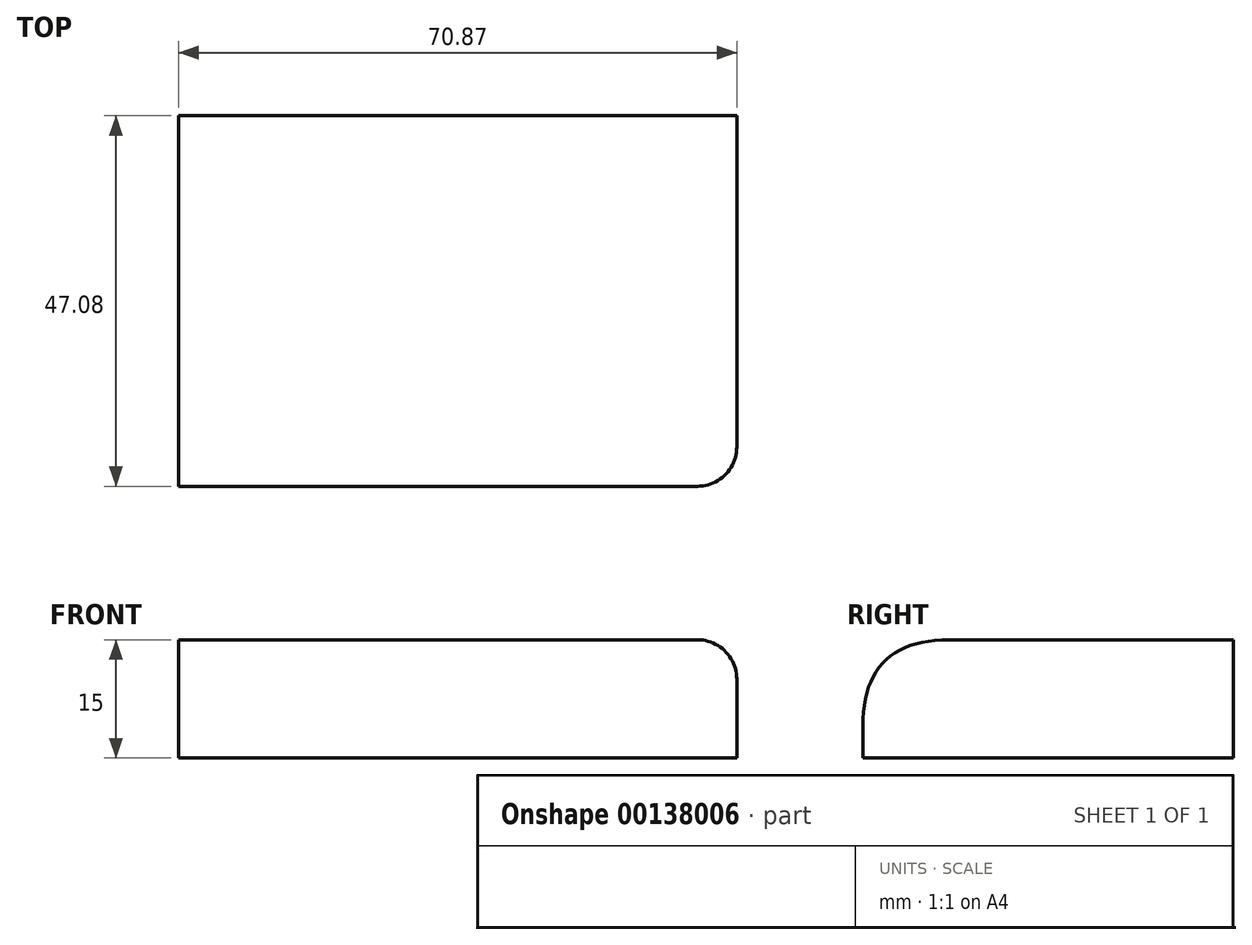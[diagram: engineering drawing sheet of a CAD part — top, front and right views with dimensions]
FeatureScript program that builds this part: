
annotation { "Feature Type Name" : "Feature", "Feature Type Description" : "" }
export const myFeature = defineFeature(function(context is Context, id is Id, definition is map)
    precondition{}
    {
        {
            var Q0;
            Q0=qCreatedBy(makeId("Top.planeOp"),FACE);
            var sketch = newSketch(context, id + "F0", { "sketchPlane" : qUnion([Q0])});
            skLineSegment(sketch, "E0.bottom", {"start": v(-36.05, -47.08) * mm, "end": v(34.82, -47.08) * mm});
            skLineSegment(sketch, "E0.top", {"start": v(-36.05, 0) * mm, "end": v(34.82, 0) * mm});
            skLineSegment(sketch, "E0.left", {"start": v(-36.05, -47.08) * mm, "end": v(-36.05, 0) * mm});
            skLineSegment(sketch, "E0.right", {"start": v(34.82, -47.08) * mm, "end": v(34.82, 0) * mm});
            skSolve(sketch);
        }
        {
            var Q0;
            Q0 = qSketchRegion(id + "F0", true);
            extrude(context, id + "F1", {"entities" : qUnion([Q0]), "depth" : 15 * mm});
        }
        {
            var Q0;
            Q0=makeQuery(id+"F1.opExtrude","CAP_EDGE",EDGE,{"disambiguationData":[OSD([sQuery(id+"F0.wireOp",EDGE,"E0.bottom")])],"isStart":false});
            fillet(context, id + "F2", {"entities" : qUnion([Q0]), "radius" : 11 * mm, "tangentPropagation" : true, "rho" : 0.5, "crossSection" : FilletCrossSection.CONIC, "allowEdgeOverflow" : false});
        }
        {
            var Q0;
            Q0=makeQuery(id+"F2.opFillet","BLEND_EDGE",EDGE,{"blendedFrom":[makeQuery(id+"F1.opExtrude","CAP_EDGE",EDGE,{"disambiguationData":[OSD([sQuery(id+"F0.wireOp",EDGE,"E0.bottom")])],"isStart":false}),makeQuery(id+"F1.opExtrude","SWEPT_FACE",FACE,{"disambiguationData":[OSD([sQuery(id+"F0.wireOp",EDGE,"E0.right")])]})],"blendedInto":[makeQuery(id+"F1.opExtrude","SWEPT_FACE",FACE,{"disambiguationData":[OSD([sQuery(id+"F0.wireOp",EDGE,"E0.right")])]})]});
            fillet(context, id + "F3", {"entities" : qUnion([Q0]), "radius" : 5 * mm, "tangentPropagation" : true, "allowEdgeOverflow" : false});
        }
    });
